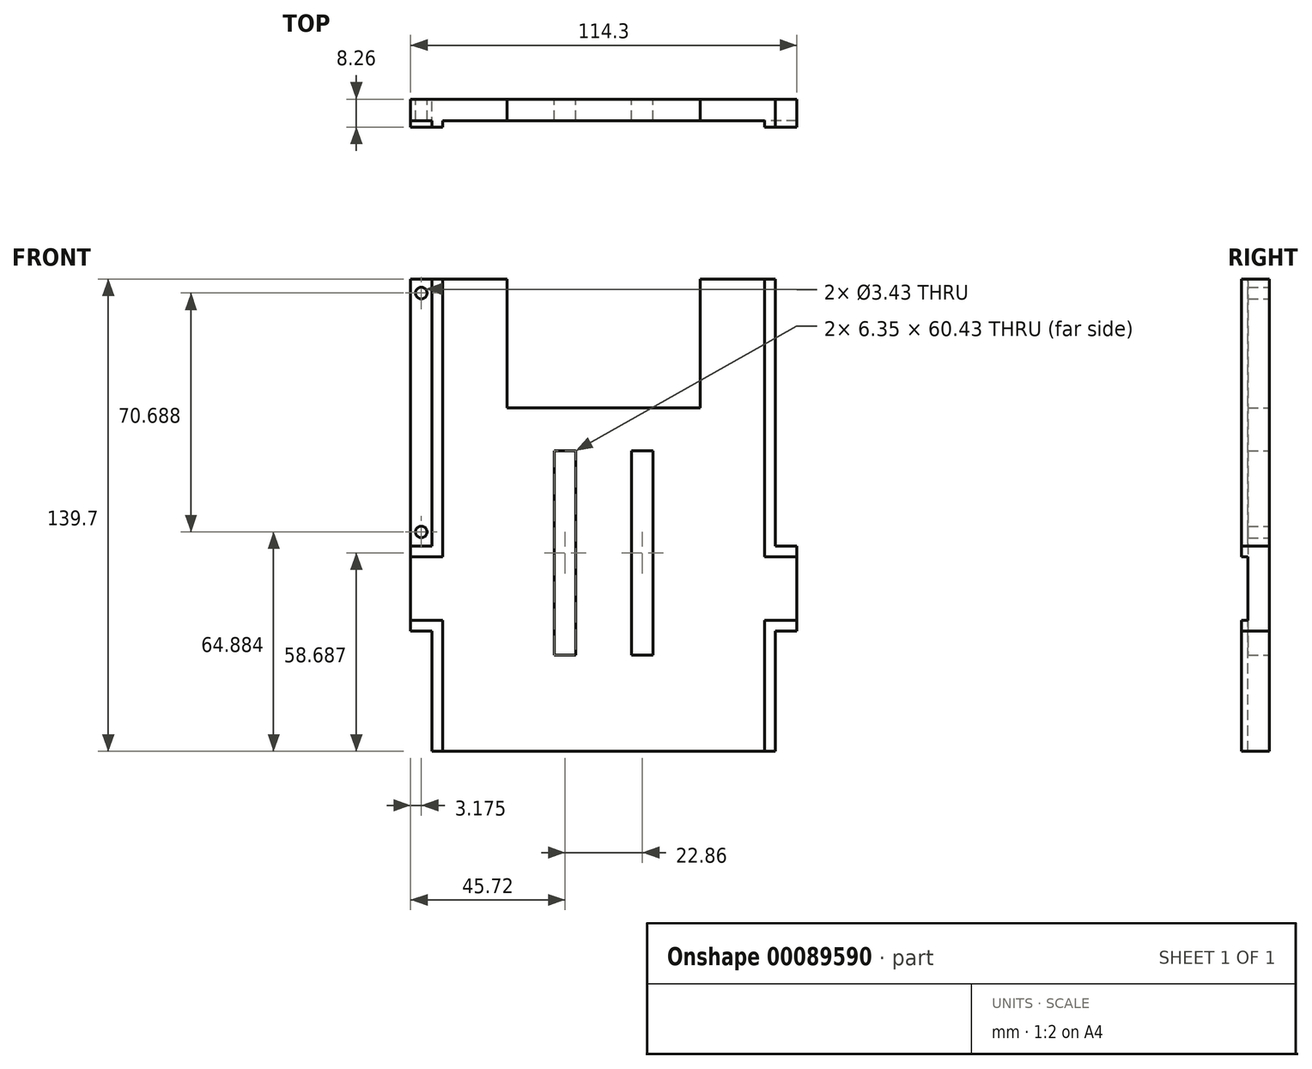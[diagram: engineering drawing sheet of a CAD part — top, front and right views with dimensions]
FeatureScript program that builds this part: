
annotation { "Feature Type Name" : "Feature", "Feature Type Description" : "" }
export const myFeature = defineFeature(function(context is Context, id is Id, definition is map)
    precondition{}
    {
        {
            var Q0;
            Q0=qCreatedBy(makeId("Front.planeOp"),FACE);
            var sketch = newSketch(context, id + "F0", { "sketchPlane" : qUnion([Q0])});
            skLineSegment(sketch, "E0.bottom", {"start": v(57.15, -69.85) * mm, "end": v(-57.15, -69.85) * mm});
            skLineSegment(sketch, "E0.top", {"start": v(57.15, 69.85) * mm, "end": v(28.57, 69.85) * mm});
            skLineSegment(sketch, "E0.left", {"start": v(57.15, -69.85) * mm, "end": v(57.15, 69.85) * mm});
            skLineSegment(sketch, "E0.right", {"start": v(-57.15, -69.85) * mm, "end": v(-57.15, 69.85) * mm});
            skPoint(sketch, "E0.middle", {"position": v(0, 0) * mm});
            skLineSegment(sketch, "E1.bottom", {"start": v(-57.15, -69.85) * mm, "end": v(-50.8, -69.85) * mm});
            skLineSegment(sketch, "E1.top", {"start": v(-57.15, -34.3) * mm, "end": v(-50.8, -34.3) * mm});
            skLineSegment(sketch, "E1.left", {"start": v(-57.15, -69.85) * mm, "end": v(-57.15, -34.3) * mm});
            skLineSegment(sketch, "E1.right", {"start": v(-50.8, -69.85) * mm, "end": v(-50.8, -34.3) * mm});
            skLineSegment(sketch, "E2.bottom", {"start": v(57.15, -69.85) * mm, "end": v(50.8, -69.85) * mm});
            skLineSegment(sketch, "E2.top", {"start": v(57.15, -34.29) * mm, "end": v(50.8, -34.29) * mm});
            skLineSegment(sketch, "E2.left", {"start": v(57.15, -69.85) * mm, "end": v(57.15, -34.29) * mm});
            skLineSegment(sketch, "E2.right", {"start": v(50.8, -69.85) * mm, "end": v(50.8, -34.3) * mm});
            skLineSegment(sketch, "E3.bottom", {"start": v(-57.15, 69.85) * mm, "end": v(-50.8, 69.85) * mm});
            skLineSegment(sketch, "E3.top", {"start": v(-57.15, -9.1) * mm, "end": v(-50.8, -9.1) * mm});
            skLineSegment(sketch, "E3.left", {"start": v(-57.15, 69.85) * mm, "end": v(-57.15, -9.1) * mm});
            skLineSegment(sketch, "E3.right", {"start": v(-50.8, 69.85) * mm, "end": v(-50.8, -9.1) * mm});
            skLineSegment(sketch, "E4.bottom", {"start": v(57.15, 69.85) * mm, "end": v(50.8, 69.85) * mm});
            skLineSegment(sketch, "E4.top", {"start": v(57.15, -9.1) * mm, "end": v(50.8, -9.1) * mm});
            skLineSegment(sketch, "E4.left", {"start": v(57.15, 69.85) * mm, "end": v(57.15, -9.1) * mm});
            skLineSegment(sketch, "E4.right", {"start": v(50.8, 69.85) * mm, "end": v(50.8, -9.1) * mm});
            skLineSegment(sketch, "E5.top", {"start": v(-28.58, 31.75) * mm, "end": v(28.58, 31.75) * mm});
            skLineSegment(sketch, "E5.left", {"start": v(-28.58, 69.85) * mm, "end": v(-28.58, 31.75) * mm});
            skLineSegment(sketch, "E5.right", {"start": v(28.58, 69.85) * mm, "end": v(28.58, 31.75) * mm});
            skLineSegment(sketch, "E6.trimOffspring", {"start": v(-28.58, 69.85) * mm, "end": v(-57.15, 69.85) * mm});
            skPoint(sketch, "E7", {"position": v(0, 31.75) * mm});
            skLineSegment(sketch, "E8.0", {"start": v(-47.63, -69.85) * mm, "end": v(-47.63, -31.12) * mm});
            skLineSegment(sketch, "E8.1", {"start": v(-57.15, -31.12) * mm, "end": v(-47.63, -31.12) * mm});
            skLineSegment(sketch, "E9.0", {"start": v(47.63, -69.85) * mm, "end": v(47.62, -31.12) * mm});
            skLineSegment(sketch, "E9.1", {"start": v(57.15, -31.12) * mm, "end": v(47.62, -31.12) * mm});
            skLineSegment(sketch, "E10.0", {"start": v(-47.63, 69.85) * mm, "end": v(-47.63, -12.27) * mm});
            skLineSegment(sketch, "E10.1", {"start": v(-57.15, -12.27) * mm, "end": v(-47.63, -12.27) * mm});
            skLineSegment(sketch, "E11.0", {"start": v(47.62, 69.85) * mm, "end": v(47.62, -12.27) * mm});
            skLineSegment(sketch, "E11.1", {"start": v(57.15, -12.27) * mm, "end": v(47.62, -12.27) * mm});
            skLineSegment(sketch, "E12", {"start": v(-53.98, -34.3) * mm, "end": v(-53.98, -69.85) * mm, "construction": true});
            skPoint(sketch, "E13", {"position": v(-53.97, -65.72) * mm});
            skPoint(sketch, "E14", {"position": v(-53.97, -38.42) * mm});
            skCircle(sketch, "E15", {"center": v(-53.97, -38.42) * mm, "radius": 1.71 * mm});
            skCircle(sketch, "E16", {"center": v(-53.97, -65.72) * mm, "radius": 1.71 * mm});
            skCircle(sketch, "E17.MirrorC", {"center": v(-53.98, -65.72) * mm, "radius": 1.71 * mm});
            skCircle(sketch, "E18.MirrorC", {"center": v(-53.98, -38.42) * mm, "radius": 1.71 * mm});
            skCircle(sketch, "E19.MirrorC", {"center": v(53.98, -38.42) * mm, "radius": 1.71 * mm});
            skLineSegment(sketch, "E20.MirrorCS", {"start": v(53.98, -34.3) * mm, "end": v(53.98, -69.85) * mm, "construction": true});
            skCircle(sketch, "E21.MirrorC", {"center": v(53.97, -65.72) * mm, "radius": 1.71 * mm});
            skLineSegment(sketch, "E22", {"start": v(-53.98, 69.85) * mm, "end": v(-53.98, -9.1) * mm, "construction": true});
            skPoint(sketch, "E23", {"position": v(-53.98, 65.72) * mm});
            skPoint(sketch, "E24", {"position": v(-53.98, -4.97) * mm});
            skCircle(sketch, "E25", {"center": v(-53.98, 65.72) * mm, "radius": 1.71 * mm});
            skCircle(sketch, "E26", {"center": v(-53.98, -4.97) * mm, "radius": 1.71 * mm});
            skCircle(sketch, "E27.MirrorC", {"center": v(53.98, 65.72) * mm, "radius": 1.71 * mm});
            skLineSegment(sketch, "E28.MirrorCS", {"start": v(53.98, 69.85) * mm, "end": v(53.98, -9.1) * mm, "construction": true});
            skPoint(sketch, "E29.MirrorP", {"position": v(53.98, -4.97) * mm});
            skCircle(sketch, "E30.MirrorC", {"center": v(53.98, -4.97) * mm, "radius": 1.71 * mm});
            skLineSegment(sketch, "E31.bottom", {"start": v(-14.6, 19.05) * mm, "end": v(-8.26, 19.05) * mm});
            skLineSegment(sketch, "E31.top", {"start": v(-14.6, -41.38) * mm, "end": v(-8.25, -41.38) * mm});
            skLineSegment(sketch, "E31.left", {"start": v(-14.6, 19.05) * mm, "end": v(-14.6, -41.38) * mm});
            skLineSegment(sketch, "E31.right", {"start": v(-8.26, 19.05) * mm, "end": v(-8.26, -41.38) * mm});
            skLineSegment(sketch, "E32.MirrorCS", {"start": v(8.26, 19.05) * mm, "end": v(8.26, -41.38) * mm});
            skLineSegment(sketch, "E33.MirrorCS", {"start": v(14.6, 19.05) * mm, "end": v(8.26, 19.05) * mm});
            skLineSegment(sketch, "E34.MirrorCS", {"start": v(14.6, 19.05) * mm, "end": v(14.6, -41.38) * mm});
            skLineSegment(sketch, "E35.MirrorCS", {"start": v(14.6, -41.38) * mm, "end": v(8.26, -41.38) * mm});
            skLineSegment(sketch, "E36", {"start": v(-11.43, -41.38) * mm, "end": v(-11.43, 19.05) * mm, "construction": true});
            skLineSegment(sketch, "E37", {"start": v(-14.6, -11.16) * mm, "end": v(-8.26, -11.16) * mm, "construction": true});
            skLineSegment(sketch, "E38.bottom", {"start": v(-8.26, -38.2) * mm, "end": v(-14.6, -38.2) * mm});
            skLineSegment(sketch, "E38.top", {"start": v(-8.26, 15.88) * mm, "end": v(-14.6, 15.88) * mm});
            skLineSegment(sketch, "E38.left", {"start": v(-8.26, -38.2) * mm, "end": v(-8.26, 15.88) * mm});
            skLineSegment(sketch, "E38.right", {"start": v(-14.6, -38.2) * mm, "end": v(-14.6, 15.88) * mm});
            skPoint(sketch, "E38.middle", {"position": v(-11.43, -11.16) * mm});
            skLineSegment(sketch, "E39.MirrorCS", {"start": v(8.26, 15.88) * mm, "end": v(14.6, 15.88) * mm});
            skLineSegment(sketch, "E40.MirrorCS", {"start": v(8.26, -38.2) * mm, "end": v(14.6, -38.2) * mm});
            skLineSegment(sketch, "E41.MirrorCS", {"start": v(11.43, -41.38) * mm, "end": v(11.43, 19.05) * mm, "construction": true});
            skCircle(sketch, "E42", {"center": v(-11.43, 15.88) * mm, "radius": 1.71 * mm});
            skCircle(sketch, "E43.MirrorC", {"center": v(-11.43, -38.2) * mm, "radius": 1.71 * mm});
            skCircle(sketch, "E44.MirrorC", {"center": v(11.43, 15.88) * mm, "radius": 1.71 * mm});
            skCircle(sketch, "E45.MirrorC", {"center": v(11.43, -38.2) * mm, "radius": 1.71 * mm});
            skSolve(sketch);
        }
        {
            var Q0;
            Q0=makeQuery(id+"F0.imprint","IMPRINT",FACE,{"disambiguationData":[TD([[makeQuery(id+"F0.imprint","IMPRINT",EDGE,{"derivedFrom":sQuery(id+"F0.wireOp",EDGE,"E3.top")}),1.0]])]});
            var Q1;
            Q1=makeQuery(id+"F0.imprint","IMPRINT",FACE,{"disambiguationData":[TD([[makeQuery(id+"F0.imprint","IMPRINT",EDGE,{"derivedFrom":sQuery(id+"F0.wireOp",EDGE,"E1.bottom")}),1.0]])]});
            var Q2;
            Q2=makeQuery(id+"F0.imprint","IMPRINT",FACE,{"disambiguationData":[TD([[makeQuery(id+"F0.imprint","IMPRINT",EDGE,{"derivedFrom":sQuery(id+"F0.wireOp",EDGE,"E2.bottom")}),-1.0]])]});
            var Q3;
            Q3=makeQuery(id+"F0.imprint","IMPRINT",FACE,{"disambiguationData":[TD([[makeQuery(id+"F0.imprint","IMPRINT",EDGE,{"derivedFrom":sQuery(id+"F0.wireOp",EDGE,"E4.bottom")}),1.0]])]});
            var Q4;
            Q4=makeQuery(id+"F0.imprint","IMPRINT",FACE,{"disambiguationData":[TD([[makeQuery(id+"F0.imprint","IMPRINT",EDGE,{"derivedFrom":sQuery(id+"F0.wireOp",EDGE,"E5.top")}),-1.0]])]});
            extrude(context, id + "F1", {"entities" : qUnion([Q0, Q1, Q2, Q3, Q4]), "depth" : 6.35 * mm});
        }
        {
            var Q0;
            {var subQ1=sQuery(id+"F0.wireOp",EDGE,"E4.top");Q0=makeQuery(id+"F0.imprint","IMPRINT",FACE,{"disambiguationData":[TD([[makeQuery(id+"F0.imprint","IMPRINT",EDGE,{"derivedFrom":subQ1}),1.0]])]});}
            var Q1;
            {var subQ0=sQuery(id+"F0.wireOp",EDGE,"E2.top");Q1=makeQuery(id+"F0.imprint","IMPRINT",FACE,{"disambiguationData":[TD([[makeQuery(id+"F0.imprint","IMPRINT",EDGE,{"derivedFrom":subQ0}),-1.0]])]});}
            var Q2;
            {var subQ3=sQuery(id+"F0.wireOp",EDGE,"E3.top");Q2=makeQuery(id+"F0.imprint","IMPRINT",FACE,{"disambiguationData":[TD([[makeQuery(id+"F0.imprint","IMPRINT",EDGE,{"derivedFrom":subQ3}),-1.0]])]});}
            var Q3;
            {var subQ1=sQuery(id+"F0.wireOp",EDGE,"E1.top");Q3=makeQuery(id+"F0.imprint","IMPRINT",FACE,{"disambiguationData":[TD([[makeQuery(id+"F0.imprint","IMPRINT",EDGE,{"derivedFrom":subQ1}),1.0]])]});}
            extrude(context, id + "F2", {"entities" : qUnion([Q0, Q1, Q2, Q3]), "operationType" : NewBodyOperationType.ADD, "depth" : 8.25 * mm});
        }
        {
            var Q0;
            Q0=makeQuery(id+"F1.opExtrude","CAP_FACE",FACE,{"disambiguationData":[OSD([sQuery(id+"F0.wireOp",EDGE,"E3.top"),sQuery(id+"F0.wireOp",EDGE,"E3.left"),sQuery(id+"F0.wireOp",EDGE,"E3.right"),sQuery(id+"F0.wireOp",EDGE,"E6.trimOffspring")])],"isStart":false});
            var sketch = newSketch(context, id + "F3", { "sketchPlane" : qUnion([Q0])});
            skSolve(sketch);
        }
    });
